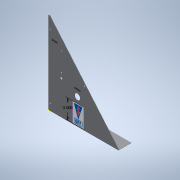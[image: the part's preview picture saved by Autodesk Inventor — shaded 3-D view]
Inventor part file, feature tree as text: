
AUTODESK INVENTOR PART (.ipt)
format: ipt  version: 2021 (Build 250183000, 183)  size: 241,152 bytes
history: native  units: in
note: dims shown in document units (in); Inventor stores cm internally (conversion verified against a paired STEP export)
features: sketch x7, extrude x6, fillet x2, other x1
ambient origin geometry x8: Origin, YZ Plane, XZ Plane, XY Plane, X Axis, Y Axis, Z Axis, Center Point
bodies: Solid1 (feature_tree)
feature tree (16):
  extrude  "Extrusion1"  Depth=0.063in
  extrude  "Extrusion2"  Depth=1.0in TaperAngle=0.0deg
  extrude  "Extrusion3"  Depth=0.126in
  extrude  "Extrusion4"  Depth=1.0in
  extrude  "Extrusion5"  Depth=10.0in
  extrude  "Extrusion6"  Depth=9.0in
  sketch  "Sketch7"  dims[d25=0.35in d26=9.0in d27=0.35in d30=0.19in]
  sketch  "Sketch8"  dims[d31=0.19in d32=0.19in d33=0.25in d34=0.0in d35=1.94in d36=11.0in d37=0.06in d38=0.0in d39=1.0in d40=0.5in d41=1.0in d42=1.25in d43=0.25in d44=0.0in d46=3.0in d57=0.125in d59=5.25in d60=1.25in d61=0.3125in d65=7.5in d66=0.35in d67=0.19in d68=0.125in]
  fillet  "Fillet1"  Radius=0.35in
  fillet  "Fillet3"  Radius=0.19in
  sketch  "Sketch1"  dims[d2=0.063in d3=0.0in d4=0.875in]
  sketch  "Sketch3"  dims[d7=1.0in d8=0.0in d15=1.0in d16=0.0in]
  sketch  "Sketch4"  dims[d19=0.126in d20=0.0709in]
  sketch  "Sketch5"  dims[d21=3.0in d22=1.0in]
  sketch  "Sketch6"  dims[d23=0.35in d24=10.0in]
  other  "Image1"
